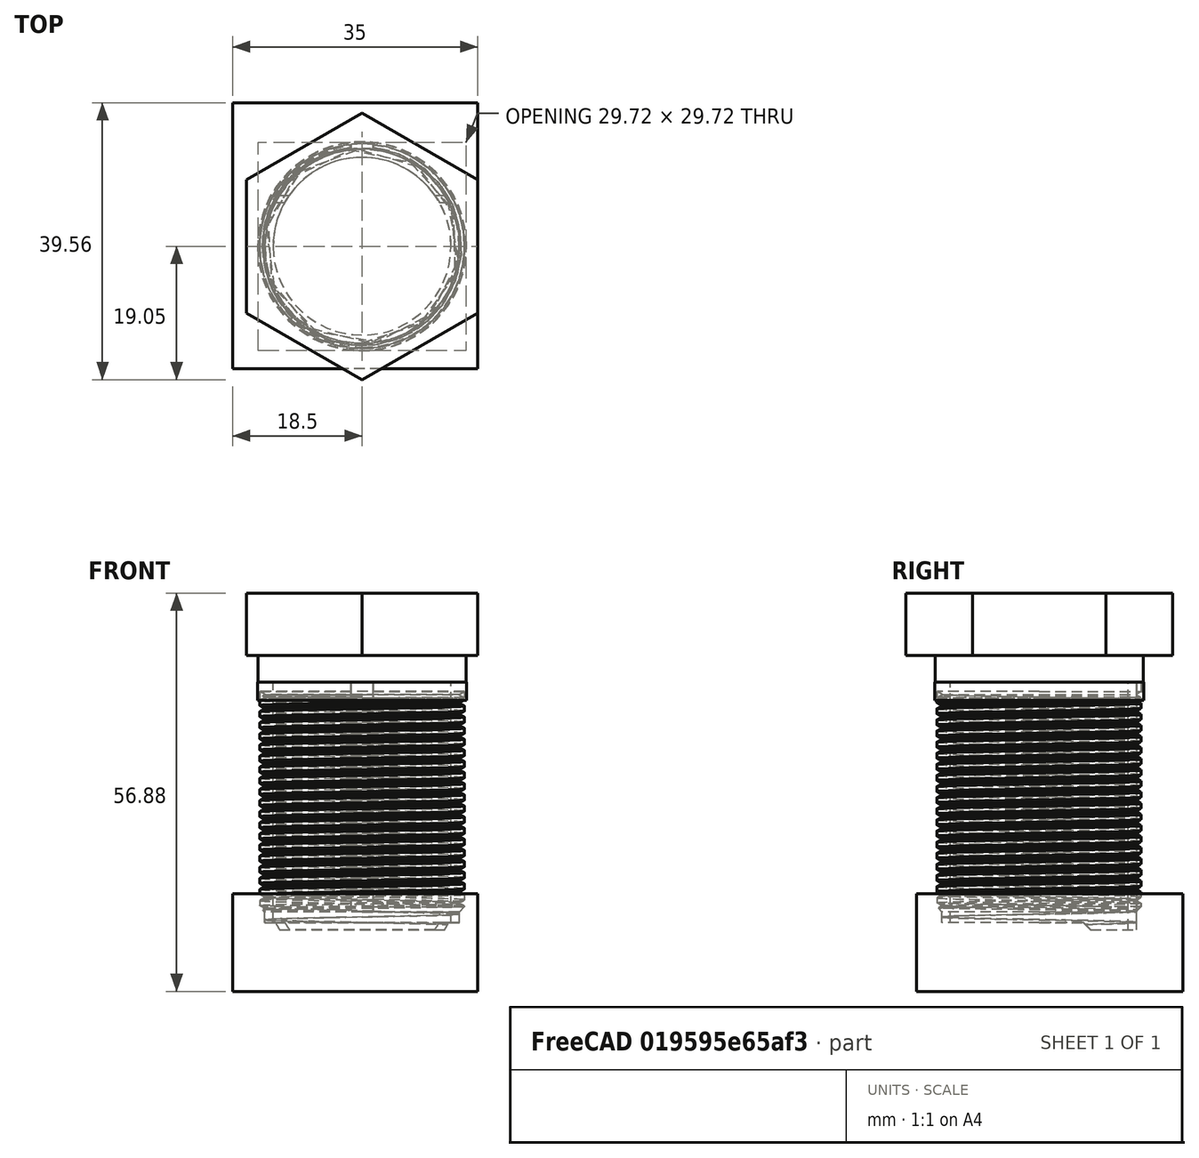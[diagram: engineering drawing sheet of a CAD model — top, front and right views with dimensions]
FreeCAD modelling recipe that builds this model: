
FCSTD DOCUMENT  (FreeCAD 0.14R3700 (Git))
Label: buffer retainer bolt
License: CC-BY 3.0
LicenseURL: http://creativecommons.org/licenses/by/3.0/
objects: Part::Feature×1, Sketcher::SketchObject×1, PartDesign::Pocket×1
note: 4 computed .brp shape members not serialized (recipe doc carries the construction recipe); baked Part::Feature solids carry a one-line shape summary decoded from their .brp

FEATURE [Part::Feature] Part__Feature  label="MAINSPRING_BUFFER_BOLT"
  shape: bbox 33 x 38.1 x 48.06 mm, 201 faces (baked)
FEATURE [Sketcher::SketchObject] Sketch
  Placement = pos=(16.4978,0,0) rot=(0.57735,0.57735,0.57735;2.0944rad)
  Support = -> Part__Feature [Face79]
  sketch-geometry (4):
    g0: LineSegment StartX=20.5106 StartY=-208.847 StartZ=0 EndX=-17.5139 EndY=-208.847 EndZ=0
    g1: LineSegment StartX=-17.5139 StartY=-208.847 StartZ=0 EndX=-17.5139 EndY=-194.905 EndZ=0
    g2: LineSegment StartX=-17.5139 StartY=-194.905 StartZ=0 EndX=20.5106 EndY=-194.905 EndZ=0
    g3: LineSegment StartX=20.5106 StartY=-194.905 StartZ=0 EndX=20.5106 EndY=-208.847 EndZ=0
  constraints (9):
    c: Coincident(g0,g1)
    c: Coincident(g1,g2)
    c: Coincident(g2,g3)
    c: Coincident(g3,g0)
    c: Horizontal(g0)
    c: Horizontal(g2)
    c: Vertical(g1)
    c: Vertical(g3)
    c: DistanceY(g-1,g1) = -194.905
FEATURE [PartDesign::Pocket] Pocket
  Length = 35
  Sketch = -> Sketch
  Type = 0
